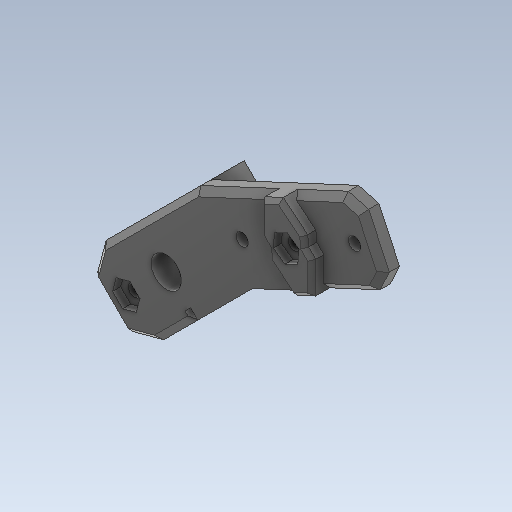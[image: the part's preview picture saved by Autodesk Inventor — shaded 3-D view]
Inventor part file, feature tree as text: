
AUTODESK INVENTOR PART (.ipt)
format: ipt  version: 2020 (Build 240168000, 168)  size: 290,304 bytes
history: native  units: in
note: dims shown in document units (in); Inventor stores cm internally (conversion verified against a paired STEP export)
features: sketch x12, other x3
ambient origin geometry x8: Origin, YZ Plane, XZ Plane, XY Plane, X Axis, Y Axis, Z Axis, Center Point
bodies: Solid1 (feature_tree)
feature tree (15):
  other  "TibiaBot.ipt"
  other  "Solid1::TibiaBot.ipt"
  other  "TaggingFeature1"
  sketch  "Sketch1"  dims[d0=0.3937in]
  sketch  "Sketch9"
  sketch  "Sketch10"
  sketch  "Sketch11"
  sketch  "Sketch15"
  sketch  "Sketch25"
  sketch  "Sketch26"
  sketch  "Sketch8"
  sketch  "Sketch12"
  sketch  "Sketch13"
  sketch  "Sketch19"
  sketch  "Sketch20"
